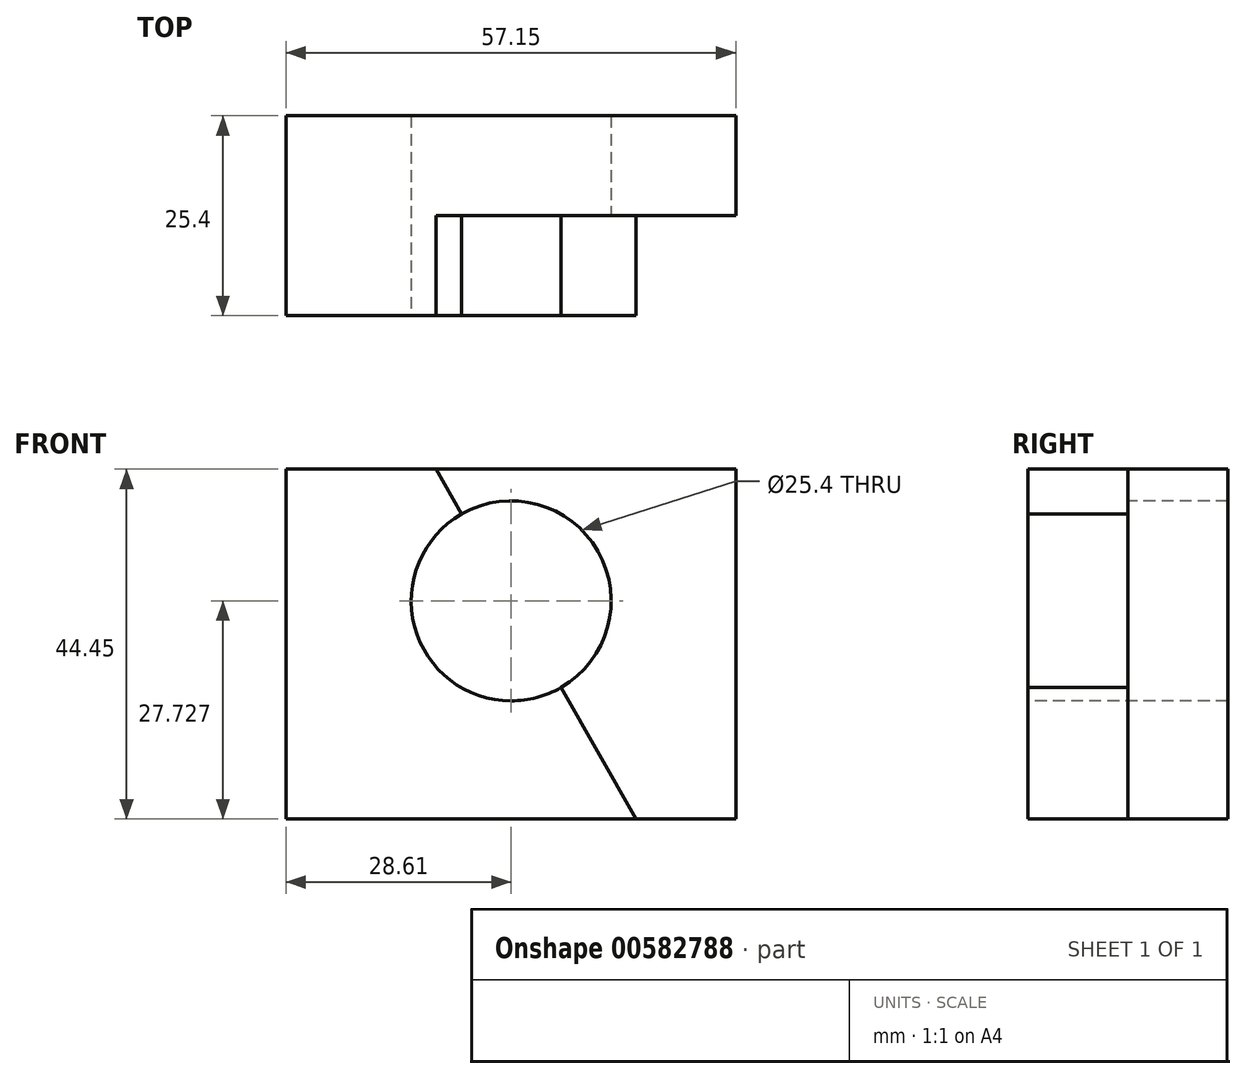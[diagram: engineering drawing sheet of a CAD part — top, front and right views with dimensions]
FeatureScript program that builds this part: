
annotation { "Feature Type Name" : "Feature", "Feature Type Description" : "" }
export const myFeature = defineFeature(function(context is Context, id is Id, definition is map)
    precondition{}
    {
        {
            var Q0;
            Q0=qCreatedBy(makeId("Front.planeOp"),FACE);
            var sketch = newSketch(context, id + "F0", { "sketchPlane" : qUnion([Q0])});
            skLineSegment(sketch, "E0", {"start": v(-28.6, 39.71) * mm, "end": v(28.54, 39.71) * mm});
            skLineSegment(sketch, "E1", {"start": v(28.54, 39.71) * mm, "end": v(28.54, -4.74) * mm});
            skLineSegment(sketch, "E2", {"start": v(28.54, -4.74) * mm, "end": v(-28.6, -4.74) * mm});
            skLineSegment(sketch, "E3", {"start": v(-28.6, -4.74) * mm, "end": v(-28.6, 39.71) * mm});
            skSolve(sketch);
        }
        {
            var Q0;
            Q0 = qSketchRegion(id + "F0", true);
            extrude(context, id + "F1", {"entities" : qUnion([Q0]), "depth" : 25.4 * mm, "offsetDistance" : 25.4 * mm});
        }
        {
            var Q0;
            Q0=makeQuery(id+"F1.opExtrude","CAP_FACE",FACE,{"disambiguationData":[OSD([sQuery(id+"F0.wireOp",EDGE,"E0"),sQuery(id+"F0.wireOp",EDGE,"E1"),sQuery(id+"F0.wireOp",EDGE,"E2"),sQuery(id+"F0.wireOp",EDGE,"E3")])],"isStart":false});
            var sketch = newSketch(context, id + "F2", { "sketchPlane" : qUnion([Q0])});
            skLineSegment(sketch, "E4", {"start": v(-9.56, 39.71) * mm, "end": v(15.84, -4.74) * mm});
            skSolve(sketch);
        }
        {
            var Q0;
            {var subQ0=sQuery(id+"F2.wireOp",EDGE,"E4");Q0=makeQuery(id+"F2.imprint","IMPRINT",FACE,{"disambiguationData":[TD([[makeQuery(id+"F2.imprint","IMPRINT",EDGE,{"derivedFrom":subQ0}),1.0]])]});}
            extrude(context, id + "F3", {"entities" : qUnion([Q0]), "operationType" : NewBodyOperationType.REMOVE, "oppositeDirection" : true, "depth" : 12.7 * mm, "offsetDistance" : 25.4 * mm});
        }
        {
            var Q0;
            Q0=makeQuery(id+"F1.opExtrude","CAP_FACE",FACE,{"disambiguationData":[OSD([sQuery(id+"F0.wireOp",EDGE,"E0"),sQuery(id+"F0.wireOp",EDGE,"E1"),sQuery(id+"F0.wireOp",EDGE,"E2"),sQuery(id+"F0.wireOp",EDGE,"E3")])],"isStart":false});
            var sketch = newSketch(context, id + "F4", { "sketchPlane" : qUnion([Q0])});
            skCircle(sketch, "E5", {"center": v(0, 22.99) * mm, "radius": 12.7 * mm});
            skSolve(sketch);
        }
        {
            var Q0;
            Q0 = qSketchRegion(id + "F4", true);
            extrude(context, id + "F5", {"entities" : qUnion([Q0]), "operationType" : NewBodyOperationType.REMOVE, "oppositeDirection" : true, "depth" : 27940 * mm, "offsetDistance" : 25.4 * mm});
        }
    });
